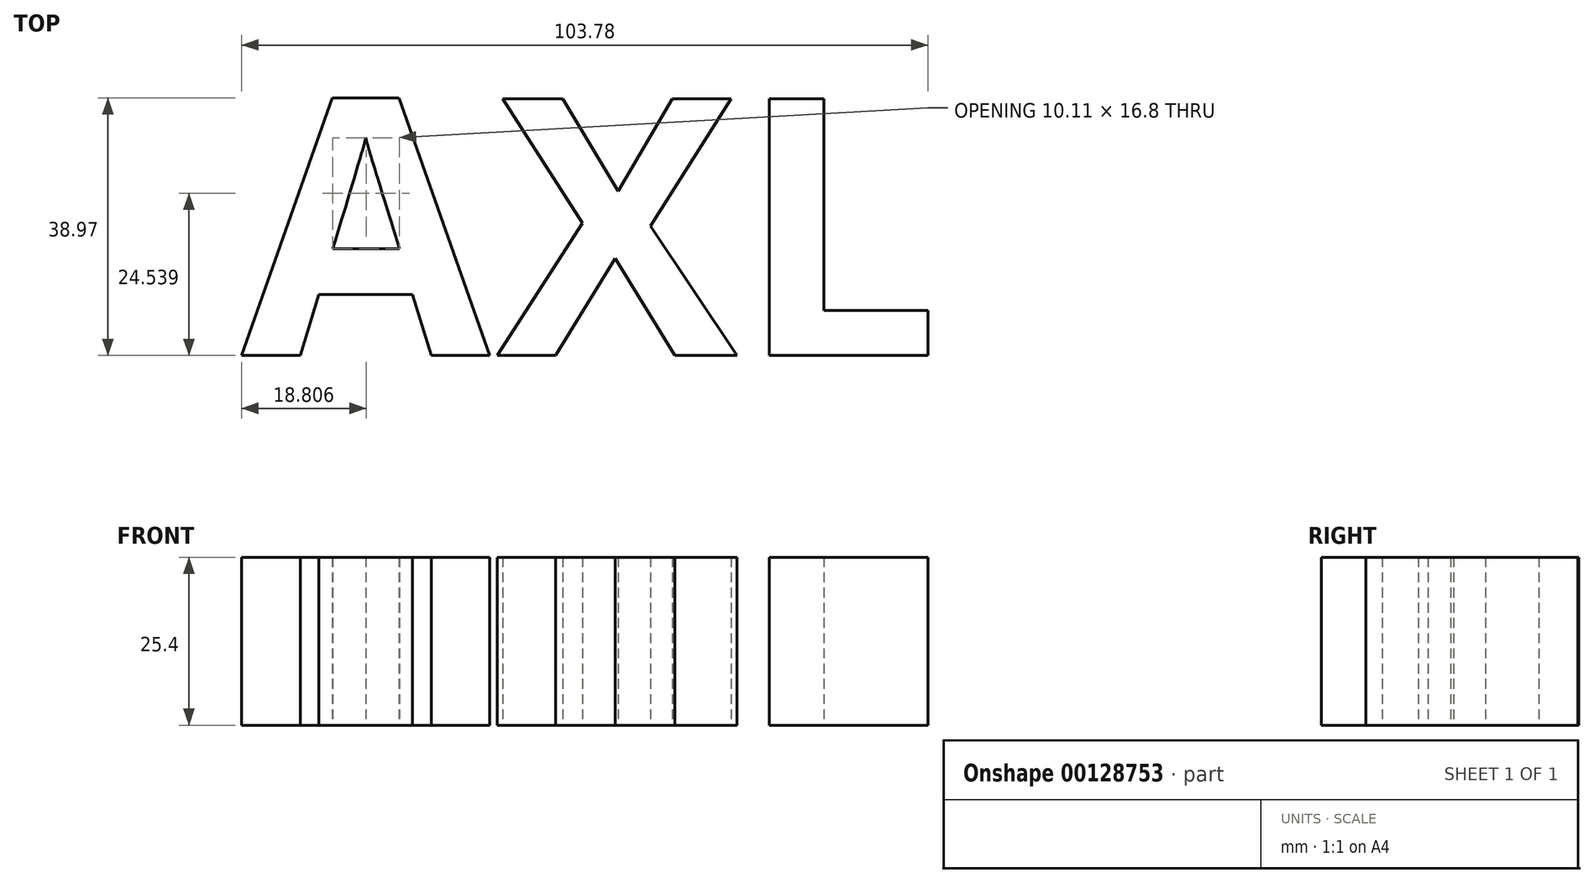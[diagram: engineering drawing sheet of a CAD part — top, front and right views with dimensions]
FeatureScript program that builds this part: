
annotation { "Feature Type Name" : "Feature", "Feature Type Description" : "" }
export const myFeature = defineFeature(function(context is Context, id is Id, definition is map)
    precondition{}
    {
        {
            var Q0;
            Q0=qCreatedBy(makeId("Top.planeOp"),FACE);
            var sketch = newSketch(context, id + "F0", { "sketchPlane" : qUnion([Q0])});
            skText(sketch, "E0", { "text": "AXL", "fontName": "OpenSans-Bold.ttf"});
            const initialGuessF0  = {"E0": [-0.06397, 0, 1, 0, 0.03914]};
            skSetInitialGuess(sketch, initialGuessF0);
            skSolve(sketch);
        }
        {
            var Q0;
            Q0=makeQuery(id+"F0.imprint","IMPRINT",FACE,{"disambiguationData":[TD([[makeQuery(id+"F0.imprint","IMPRINT",EDGE,{"derivedFrom":sQuery(id+"F0.wireOp",EDGE,"E0.sketch_text.stroke-12")}),-1.0]])]});
            var Q1;
            Q1=makeQuery(id+"F0.imprint","IMPRINT",FACE,{"disambiguationData":[TD([[makeQuery(id+"F0.imprint","IMPRINT",EDGE,{"derivedFrom":sQuery(id+"F0.wireOp",EDGE,"E0.sketch_text.stroke-0")}),-1.0]])]});
            var Q2;
            Q2=makeQuery(id+"F0.imprint","IMPRINT",FACE,{"disambiguationData":[TD([[makeQuery(id+"F0.imprint","IMPRINT",EDGE,{"derivedFrom":sQuery(id+"F0.wireOp",EDGE,"E0.sketch_text.stroke-24")}),-1.0]])]});
            extrude(context, id + "F1", {"entities" : qUnion([Q0, Q1, Q2]), "depth" : 25.4 * mm});
        }
    });
